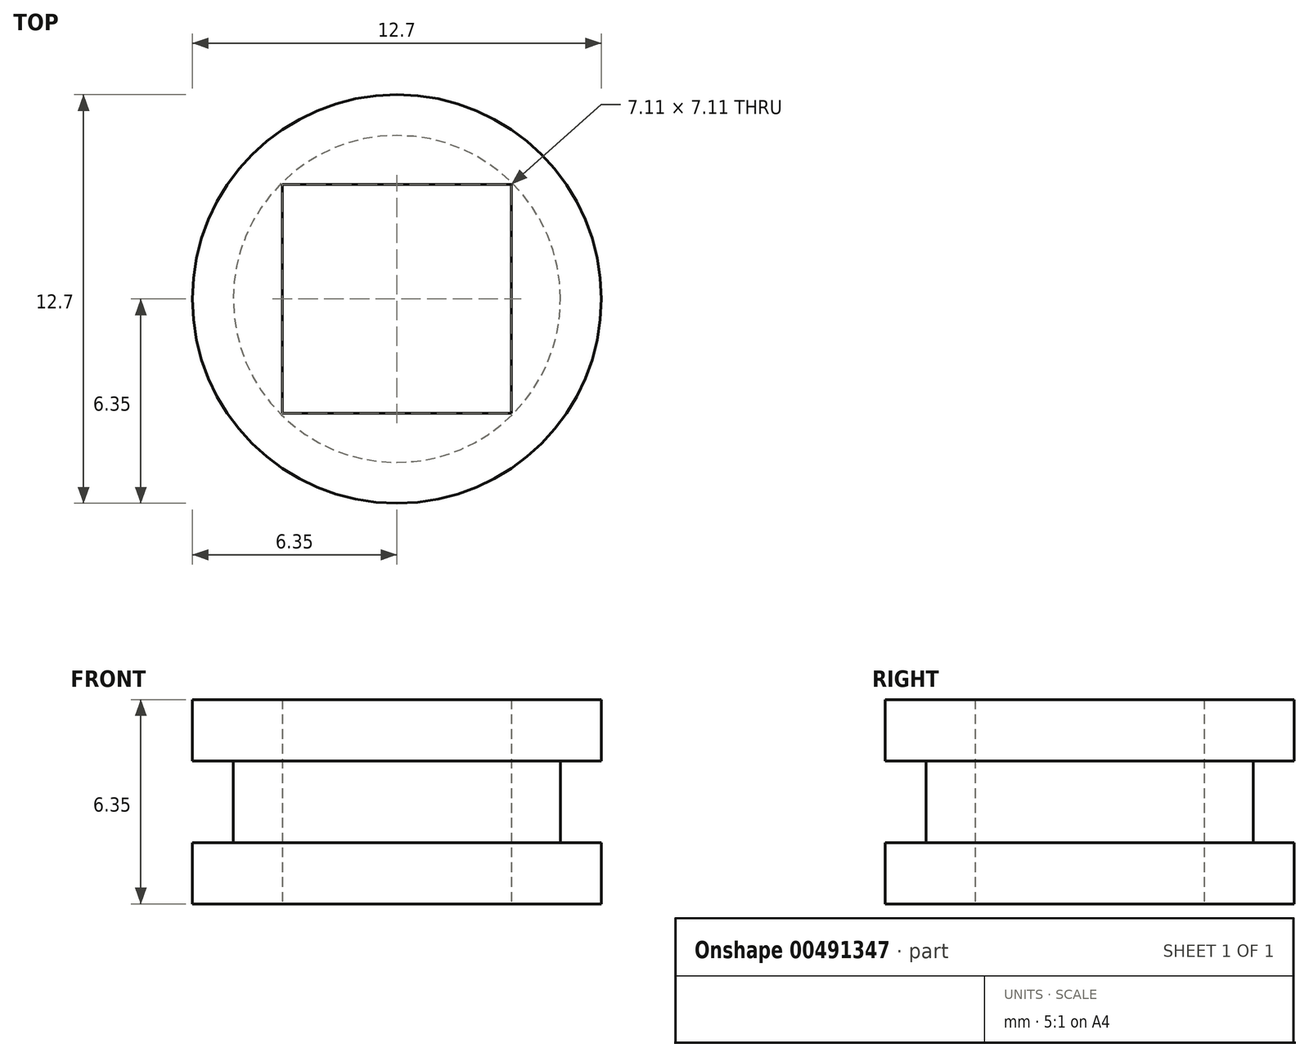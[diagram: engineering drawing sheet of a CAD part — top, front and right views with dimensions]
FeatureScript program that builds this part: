
annotation { "Feature Type Name" : "Feature", "Feature Type Description" : "" }
export const myFeature = defineFeature(function(context is Context, id is Id, definition is map)
    precondition{}
    {
        {
            var Q0;
            Q0=qCreatedBy(makeId("Front.planeOp"),FACE);
            var sketch = newSketch(context, id + "F0", { "sketchPlane" : qUnion([Q0])});
            skPoint(sketch, "E0.middle", {"position": v(0, 0) * mm});
            skLineSegment(sketch, "E1.bottom", {"start": v(0, 0) * mm, "end": v(6.35, 0) * mm});
            skLineSegment(sketch, "E1.top", {"start": v(0, 6.35) * mm, "end": v(6.35, 6.35) * mm});
            skLineSegment(sketch, "E1.left", {"start": v(0, 0) * mm, "end": v(0, 6.35) * mm});
            skLineSegment(sketch, "E1.right", {"start": v(6.35, 0) * mm, "end": v(6.35, 6.35) * mm});
            skLineSegment(sketch, "E2.bottom", {"start": v(6.35, 4.44) * mm, "end": v(5.08, 4.44) * mm});
            skLineSegment(sketch, "E2.top", {"start": v(6.35, 1.9) * mm, "end": v(5.08, 1.9) * mm});
            skLineSegment(sketch, "E2.left", {"start": v(6.35, 4.45) * mm, "end": v(6.35, 1.9) * mm});
            skLineSegment(sketch, "E2.right", {"start": v(5.08, 4.44) * mm, "end": v(5.08, 1.9) * mm});
            skSolve(sketch);
        }
        {
            var Q0;
            {var subQ1=sQuery(id+"F0.wireOp",EDGE,"E1.bottom");Q0=makeQuery(id+"F0.imprint","IMPRINT",FACE,{"disambiguationData":[TD([[makeQuery(id+"F0.imprint","IMPRINT",EDGE,{"derivedFrom":subQ1}),1.0]])]});}
            var Q1;
            Q1=sQuery(id+"F0.wireOp",EDGE,"E1.left");
            revolve(context, id + "F1", {"entities" : qUnion([Q0]), "axis" : qUnion([Q1]), "revolveType" : RevolveType.FULL});
        }
        {
            var Q0;
            Q0=makeQuery(id+"F1.opRevolve","SWEPT_FACE",FACE,{"disambiguationData":[OSD([sQuery(id+"F0.wireOp",EDGE,"E1.bottom")])]});
            var sketch = newSketch(context, id + "F2", { "sketchPlane" : qUnion([Q0])});
            skLineSegment(sketch, "E3.bottom", {"start": v(3.56, 3.56) * mm, "end": v(-3.56, 3.56) * mm});
            skLineSegment(sketch, "E3.top", {"start": v(3.56, -3.56) * mm, "end": v(-3.56, -3.56) * mm});
            skLineSegment(sketch, "E3.left", {"start": v(3.56, 3.56) * mm, "end": v(3.56, -3.56) * mm});
            skLineSegment(sketch, "E3.right", {"start": v(-3.56, 3.56) * mm, "end": v(-3.56, -3.56) * mm});
            skPoint(sketch, "E3.middle", {"position": v(0, 0) * mm});
            skSolve(sketch);
        }
        {
            var Q0;
            Q0=makeQuery(id+"F2.imprint","IMPRINT",FACE,{"disambiguationData":[TD([[makeQuery(id+"F2.imprint","IMPRINT",EDGE,{"derivedFrom":sQuery(id+"F2.wireOp",EDGE,"E3.bottom")}),1.0]])]});
            extrude(context, id + "F3", {"entities" : qUnion([Q0]), "operationType" : NewBodyOperationType.REMOVE, "oppositeDirection" : true, "depth" : 25.4 * mm});
        }
    });
